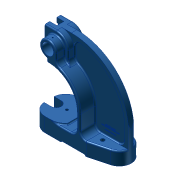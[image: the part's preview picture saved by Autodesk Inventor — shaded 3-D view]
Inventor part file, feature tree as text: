
AUTODESK INVENTOR PART (.ipt)
format: ipt  version: unknown  size: 1,460,224 bytes
history: native  units: mm (DEFAULTED — no unit token found)
features: sketch x30, fillet x27, extrude x24, projected_geometry x8, mirror x6, hole x5, plane x4, delete_face x1, emboss x1
ambient origin geometry x8: Origin, YZ Plane, XZ Plane, XY Plane, X Axis, Y Axis, Z Axis, Center Point
feature tree (106):
  extrude  "Extrusion6"  Depth=79.375mm
  extrude  "Extrusion7"  Depth=219.075mm
  sketch  "Sketch9"  dims[d53=228.6mm d54=3.175mm]
  plane  "Work Plane2"
  extrude  "Extrusion9"  Depth=3.175mm
  extrude  "Extrusion10"  Depth=76.2mm
  extrude  "Extrusion11"  Depth=25.4mm
  mirror  "Mirror3"
  extrude  "Extrusion12"  Depth=88.9mm TaperAngle=0.0deg
  extrude  "Extrusion13"  Depth=33.3248mm
  plane  "Work Plane5"
  extrude  "Extrusion14"  Depth=88.9mm TaperAngle=0.0deg
  extrude  "Extrusion15"  [1 undecoded]
  extrude  "Extrusion16"  Depth=61.8236mm
  fillet  "Fillet2"  Radius=85.725mm
  fillet  "Fillet3"  Radius=152.401053mm
  extrude  "Extrusion17"  Depth=9.525mm
  mirror  "Mirror4"
  fillet  "Fillet4"  Radius=9.525mm
  fillet  "Fillet5"  Radius=3.175mm
  fillet  "Fillet6"  Radius=31.75mm
  fillet  "Fillet7"  [1 undecoded]
  extrude  "Extrusion19"  Depth=44.45mm
  extrude  "Extrusion20"  Depth=3.175mm
  mirror  "Mirror5"
  fillet  "Fillet9"  Radius=9.525mm
  fillet  "Fillet10"  Radius=22.225mm
  fillet  "Fillet11"  Radius=44.45mm
  fillet  "Fillet12"  Radius=9.525mm
  fillet  "Fillet15"  Radius=22.225mm
  extrude  "Extrusion21"  [1 undecoded]
  extrude  "Extrusion22"  Depth=19.05mm
  fillet  "Fillet16"  Radius=12.7mm
  extrude  "Extrusion23"  Depth=30.0736mm
  plane  "Work Plane7"
  extrude  "Extrusion24"  Depth=30.0mm
  fillet  "Fillet17"  Radius=38.1mm
  hole  "Hole1"  [1 undecoded]
  hole  "Hole2"  [1 undecoded]
  extrude  "Extrusion25"  Depth=15.875mm
  fillet  "Fillet19"  Radius=3.175mm
  hole  "Hole3"  [1 undecoded]
  hole  "Hole5"  [1 undecoded]
  mirror  "Mirror6"
  hole  "Hole6"  [1 undecoded]
  extrude  "Extrusion26"  Depth=3.175mm TaperAngle=0.0deg
  plane  "Work Plane8"
  mirror  "Mirror7"
  extrude  "Extrusion27"  Depth=15.875mm
  delete_face  "Delete Face1"
  extrude  "Extrusion28"  Depth=15.875mm
  mirror  "Mirror8"
  fillet  "Fillet21"  Radius=15.875mm
  fillet  "Fillet22"  Radius=7.9248mm
  fillet  "Fillet23"  Radius=26.9875mm
  fillet  "Fillet24"  Radius=76.2mm
  fillet  "Fillet25"  Radius=65.0748mm
  fillet  "Fillet26"  Radius=3.175mm
  extrude  "Extrusion29"  Depth=3.175mm
  extrude  "Extrusion30"  Depth=50.7746mm
  fillet  "Fillet27"  Radius=12.6873mm
  fillet  "Fillet28"  [1 undecoded]
  fillet  "Fillet30"  [1 undecoded]
  extrude  "Extrusion31"  Depth=3.175mm
  fillet  "Fillet31"  Radius=31.75mm
  fillet  "Fillet32"  Radius=15.875mm
  fillet  "Fillet33"  Radius=6.35mm
  fillet  "Fillet34"  Radius=25.4mm
  emboss  "Emboss1"
  sketch  "Sketch7"  dims[d32=47.625mm d33=47.625mm d39=47.625mm d46=79.375mm]
  sketch  "Sketch8"  dims[d47=38.1mm d52=219.075mm]
  sketch  "Sketch12"  dims[d55=152.4mm d56=76.2mm]
  sketch  "Sketch13"  dims[d57=63.5mm d59=25.4mm]
  sketch  "Sketch14"  dims[d60=30.0736mm d61=88.9mm d62=0.0mm]
  sketch  "Sketch16"  dims[d63=15.0deg d64=33.3248mm]
  sketch  "Sketch17"  dims[d65=31.75mm d66=88.9mm d67=0.0mm]
  sketch  "Sketch18"  dims[d76=61.8236mm d80=-44.45mm]
  sketch  "Sketch19"  dims[d86=9.525mm d87=61.8236mm d88=85.725mm d89=152.401053mm]
  sketch  "Sketch20"  dims[d90=37.3126mm d91=0.0mm d93=9.525mm d94=9.525mm d96=3.175mm d97=0.0mm d98=31.75mm d99=0.0mm]
  sketch  "Sketch22"  dims[d100=9.525mm d101=44.45mm]
  sketch  "Sketch23"  dims[d102=30.0736mm d103=3.175mm d105=9.525mm d106=22.225mm d107=0.0mm d109=44.45mm d111=9.525mm d112=22.225mm d113=0.0mm]
  sketch  "Sketch24"  dims[d116=22.225mm d117=0.0mm d118=-22.225mm]
  projected_geometry  "Projected Loop4"
  sketch  "Sketch25"  dims[d120=38.1mm d121=19.05mm d122=12.7mm]
  sketch  "Sketch27"  dims[d123=12.7mm d124=30.0736mm]
  projected_geometry  "Projected Loop5"
  sketch  "Sketch28"  dims[d125=25.4mm d126=0.0mm d127=30.0mm d128=38.1mm d129=0.0mm]
  sketch  "Sketch29"  dims[d130=19.0754mm d131=25.4mm d132=0.0mm]
  projected_geometry  "Projected Loop6"
  sketch  "Sketch30"  dims[d134=15.875mm d135=15.875mm]
  projected_geometry  "Projected Loop7"
  sketch  "Sketch31"  dims[d136=15.0876mm d137=0.0mm d138=15.875mm d139=3.175mm]
  sketch  "Sketch32"  dims[d140=3.175mm d141=15.875mm]
  sketch  "Sketch34"  dims[d147=26.9875mm d148=19.05mm]
  sketch  "Sketch35"  dims[d149=3.175mm d150=0.0mm d151=88.9mm]
  sketch  "Sketch36"  dims[d153=28.575mm d154=3.175mm d155=0.0mm]
  projected_geometry  "Projected Loop8"
  sketch  "Sketch37"  dims[d156=3.175mm d157=15.875mm]
  sketch  "Sketch39"  dims[d158=15.875mm d159=15.875mm d162=15.875mm d163=7.9248mm d164=26.9875mm d165=0.0mm d166=76.2mm d167=65.0748mm d168=3.175mm]
  sketch  "Sketch40"  dims[d169=26.9875mm d170=0.0mm d171=3.175mm]
  projected_geometry  "Projected Loop9"
  sketch  "Sketch41"  dims[d176=60.325mm d178=50.7746mm d179=12.6873mm d180=0.0mm d181=-44.45mm d182=30.0deg]
  projected_geometry  "Projected Loop10"
  sketch  "Sketch42"  dims[d183=73.0504mm d184=0.0mm d185=3.175mm d186=31.75mm d187=15.875mm d188=6.35mm]
  projected_geometry  "Projected Loop11"
  sketch  "Sketch43"  dims[d189=4.9784mm d190=12.7mm d191=9.525mm d192=6.35mm d193=14.3117mm d194=19.1008mm d195=20.594885mm d196=25.4mm d197=9.525mm d199=3.9624mm d200=12.7mm d201=9.525mm d202=6.35mm d203=14.3117mm d204=19.05mm d205=20.594885mm d206=17.4498mm d207=9.525mm d208=0.0mm d210=3.175mm d212=3.175mm d213=12.7mm d214=9.525mm d215=6.35mm d216=14.3117mm d217=25.4mm d218=20.594885mm d228=142.875mm d229=19.05mm d230=10.3124mm d231=12.7mm d232=9.525mm d233=6.35mm d234=14.3117mm d235=12.7mm d236=20.594885mm d237=28.575mm d238=0.0mm d239=6.731mm d240=12.7mm d241=9.525mm d242=6.35mm d243=14.3117mm d244=12.7mm d245=20.594885mm d246=19.0246mm d247=9.4996mm d248=19.1008mm d249=0.0mm d250=-31.75mm d251=12.7mm d252=0.0mm d255=6.35mm d256=20.5486mm d264=25.4mm d265=0.0mm d266=3.175mm d267=3.175mm d268=3.175mm d269=3.175mm d270=3.175mm d271=3.175mm d272=3.175mm d275=11.0998mm d276=25.4mm d277=0.0mm d278=26.8986mm d279=0.0mm d280=3.175mm d281=3.175mm d283=3.175mm d284=9.525mm d285=0.0mm d286=3.175mm d287=3.175mm d288=3.175mm d289=3.175mm d290=4.7625mm d293=2.54mm d294=0.0mm]
note: 10 required parameter values undecoded (feature->parameter linkage not recoverable at this tier; creation-order binding heuristic only, values carry confidence <= 0.55)
